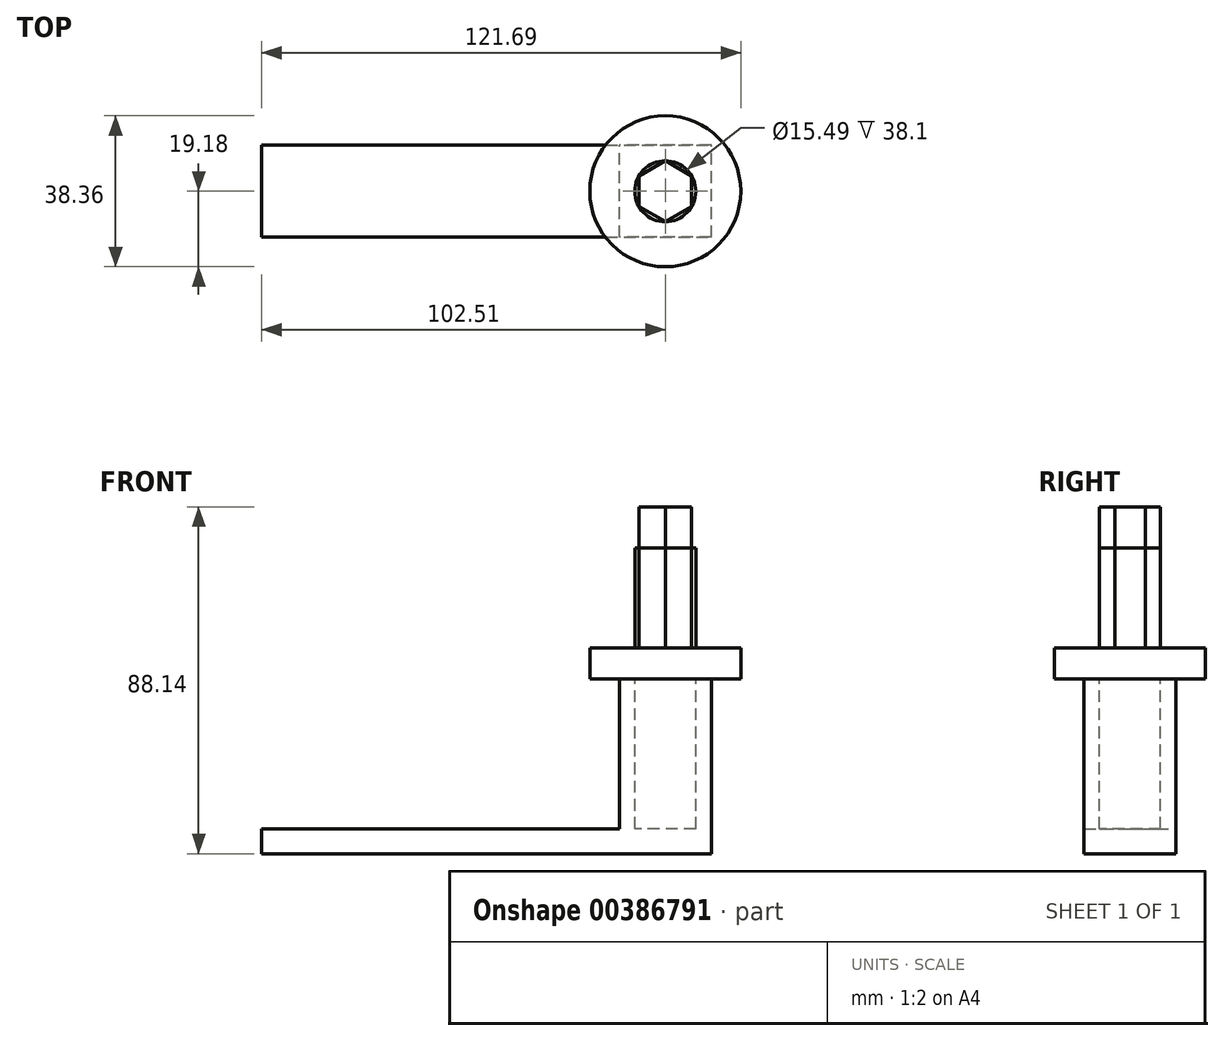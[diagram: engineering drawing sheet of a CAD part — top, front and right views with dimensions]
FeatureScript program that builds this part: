
annotation { "Feature Type Name" : "Feature", "Feature Type Description" : "" }
export const myFeature = defineFeature(function(context is Context, id is Id, definition is map)
    precondition{}
    {
        {
            var Q0;
            Q0=qCreatedBy(makeId("Top.planeOp"),FACE);
            var sketch = newSketch(context, id + "F0", { "sketchPlane" : qUnion([Q0])});
            skCircle(sketch, "E0", {"center": v(0, 0) * mm, "radius": 7.75 * mm});
            skCircle(sketch, "E1.cCircle", {"center": v(0, 0) * mm, "radius": 7.75 * mm, "construction": true});
            skLineSegment(sketch, "E1.0", {"start": v(0, 7.75) * mm, "end": v(6.7, 3.87) * mm});
            skLineSegment(sketch, "E1.1", {"start": v(6.7, 3.87) * mm, "end": v(6.7, -3.87) * mm, "construction": true});
            skLineSegment(sketch, "E1.2", {"start": v(6.7, -3.87) * mm, "end": v(0, -7.75) * mm, "construction": true});
            skLineSegment(sketch, "E1.3", {"start": v(0, -7.75) * mm, "end": v(-6.7, -3.87) * mm, "construction": true});
            skLineSegment(sketch, "E1.4", {"start": v(-6.7, -3.87) * mm, "end": v(-6.7, 3.87) * mm, "construction": true});
            skLineSegment(sketch, "E1.5", {"start": v(-6.7, 3.87) * mm, "end": v(0, 7.75) * mm, "construction": true});
            skLineSegment(sketch, "E2.bottom", {"start": v(-102.55, 11.75) * mm, "end": v(11.75, 11.75) * mm});
            skLineSegment(sketch, "E2.top", {"start": v(-102.55, -11.75) * mm, "end": v(11.75, -11.75) * mm});
            skLineSegment(sketch, "E2.left", {"start": v(-102.55, 11.75) * mm, "end": v(-102.55, -11.75) * mm});
            skLineSegment(sketch, "E2.right", {"start": v(11.75, 11.75) * mm, "end": v(11.75, -11.75) * mm});
            skCircle(sketch, "E3", {"center": v(0, 0) * mm, "radius": 19.18 * mm});
            skLineSegment(sketch, "E4.bottom", {"start": v(11.68, -11.68) * mm, "end": v(-11.68, -11.68) * mm});
            skLineSegment(sketch, "E4.top", {"start": v(11.68, 11.68) * mm, "end": v(-11.68, 11.68) * mm});
            skLineSegment(sketch, "E4.left", {"start": v(11.68, -11.68) * mm, "end": v(11.68, 11.68) * mm});
            skLineSegment(sketch, "E4.right", {"start": v(-11.68, -11.68) * mm, "end": v(-11.68, 11.68) * mm});
            skSolve(sketch);
        }
        {
            var Q0;
            {var subQ0=sQuery(id+"F0.wireOp",EDGE,"E2.right");Q0=makeQuery(id+"F0.imprint","IMPRINT",FACE,{"disambiguationData":[TD([[makeQuery(id+"F0.imprint","IMPRINT",EDGE,{"derivedFrom":subQ0}),1.0]])]});}
            var Q1;
            {var subQ0=sQuery(id+"F0.wireOp",EDGE,"E2.right");Q1=makeQuery(id+"F0.imprint","IMPRINT",FACE,{"disambiguationData":[TD([[makeQuery(id+"F0.imprint","IMPRINT",EDGE,{"derivedFrom":subQ0}),-1.0]])]});}
            var Q2;
            Q2=makeQuery(id+"F0.imprint","IMPRINT",FACE,{"disambiguationData":[TD([[makeQuery(id+"F0.imprint","IMPRINT",EDGE,{"derivedFrom":sQuery(id+"F0.wireOp",EDGE,"E4.bottom")}),-1.0]])]});
            var Q3;
            {var subQ0=sQuery(id+"F0.wireOp",EDGE,"E1.0");Q3=makeQuery(id+"F0.imprint","IMPRINT",FACE,{"disambiguationData":[TD([[makeQuery(id+"F0.imprint","IMPRINT",EDGE,{"derivedFrom":subQ0}),-1.0]])]});}
            var Q4;
            {var subQ0=sQuery(id+"F0.wireOp",EDGE,"E1.0");Q4=makeQuery(id+"F0.imprint","IMPRINT",FACE,{"disambiguationData":[TD([[makeQuery(id+"F0.imprint","IMPRINT",EDGE,{"derivedFrom":subQ0}),1.0]])]});}
            extrude(context, id + "F1", {"entities" : qUnion([Q0, Q1, Q2, Q3, Q4]), "depth" : 7.87 * mm});
        }
        {
            var Q0;
            Q0=makeQuery(id+"F1.opExtrude","CAP_FACE",FACE,{"disambiguationData":[OSD([sQuery(id+"F0.wireOp",EDGE,"E0"),sQuery(id+"F0.wireOp",EDGE,"E3")])],"isStart":false});
            var sketch = newSketch(context, id + "F2", { "sketchPlane" : qUnion([Q0])});
            skCircle(sketch, "E5", {"center": v(0, 0) * mm, "radius": 7.75 * mm});
            skCircle(sketch, "E6.cCircle", {"center": v(0, 0) * mm, "radius": 7.75 * mm, "construction": true});
            skLineSegment(sketch, "E6.0", {"start": v(0, 7.75) * mm, "end": v(6.7, 3.87) * mm});
            skLineSegment(sketch, "E6.1", {"start": v(6.7, 3.87) * mm, "end": v(6.7, -3.87) * mm});
            skLineSegment(sketch, "E6.2", {"start": v(6.7, -3.87) * mm, "end": v(0, -7.75) * mm});
            skLineSegment(sketch, "E6.3", {"start": v(0, -7.75) * mm, "end": v(-6.7, -3.87) * mm});
            skLineSegment(sketch, "E6.4", {"start": v(-6.7, -3.87) * mm, "end": v(-6.7, 3.87) * mm});
            skLineSegment(sketch, "E6.5", {"start": v(-6.7, 3.87) * mm, "end": v(0, 7.75) * mm});
            skSolve(sketch);
        }
        {
            var Q0;
            Q0=makeQuery(id+"F2.imprint","IMPRINT",FACE,{"disambiguationData":[TD([[makeQuery(id+"F2.imprint","IMPRINT",EDGE,{"derivedFrom":sQuery(id+"F2.wireOp",EDGE,"E6.0")}),-1.0]])]});
            extrude(context, id + "F3", {"entities" : qUnion([Q0]), "depth" : 35.81 * mm});
        }
        {
            var Q0;
            Q0=makeQuery(id+"F0.imprint","IMPRINT",FACE,{"disambiguationData":[TD([[makeQuery(id+"F0.imprint","IMPRINT",EDGE,{"derivedFrom":sQuery(id+"F0.wireOp",EDGE,"E4.bottom")}),-1.0]])]});
            extrude(context, id + "F4", {"entities" : qUnion([Q0]), "operationType" : NewBodyOperationType.ADD, "depth" : -38.1 * mm});
        }
        {
            var Q0;
            Q0=makeQuery(id+"F4.opExtrude","CAP_FACE",FACE,{"disambiguationData":[OSD([sQuery(id+"F0.wireOp",EDGE,"E0"),sQuery(id+"F0.wireOp",EDGE,"E4.bottom"),sQuery(id+"F0.wireOp",EDGE,"E4.top"),sQuery(id+"F0.wireOp",EDGE,"E4.left"),sQuery(id+"F0.wireOp",EDGE,"E4.right")])],"isStart":false});
            var sketch = newSketch(context, id + "F5", { "sketchPlane" : qUnion([Q0])});
            skLineSegment(sketch, "E7.bottom", {"start": v(-102.5, 11.68) * mm, "end": v(11.68, 11.68) * mm});
            skLineSegment(sketch, "E7.top", {"start": v(-102.5, -11.68) * mm, "end": v(11.68, -11.68) * mm});
            skLineSegment(sketch, "E7.left", {"start": v(-102.5, 11.68) * mm, "end": v(-102.5, -11.68) * mm});
            skLineSegment(sketch, "E7.right", {"start": v(11.68, 11.68) * mm, "end": v(11.68, -11.68) * mm});
            skSolve(sketch);
        }
        {
            var Q0;
            {var subQ2=sQuery(id+"F5.wireOp",EDGE,"E7.left");Q0=makeQuery(id+"F5.imprint","IMPRINT",FACE,{"disambiguationData":[TD([[makeQuery(id+"F5.imprint","IMPRINT",EDGE,{"derivedFrom":subQ2}),1.0]])]});}
            var Q1;
            {var subQ0=sQuery(id+"F5.wireOp",EDGE,"E7.right");Q1=makeQuery(id+"F5.imprint","IMPRINT",FACE,{"disambiguationData":[TD([[makeQuery(id+"F5.imprint","IMPRINT",EDGE,{"derivedFrom":subQ0}),-1.0]])]});}
            var Q2;
            Q2=makeQuery(id+"F5.imprint","IMPRINT",FACE,{"disambiguationData":[TD([[makeQuery(id+"F5.imprint","IMPRINT",EDGE,{"derivedFrom":makeQuery(id+"F4.opExtrude","CAP_EDGE",EDGE,{"disambiguationData":[OSD([sQuery(id+"F0.wireOp",EDGE,"E0")])],"isStart":false})}),-1.0]])]});
            extrude(context, id + "F6", {"entities" : qUnion([Q0, Q1, Q2]), "operationType" : NewBodyOperationType.ADD, "depth" : 6.35 * mm});
        }
        {
            var Q0;
            Q0=makeQuery(id+"F2.imprint","IMPRINT",FACE,{"disambiguationData":[TD([[makeQuery(id+"F2.imprint","IMPRINT",EDGE,{"derivedFrom":makeQuery(id+"F1.opExtrude","CAP_EDGE",EDGE,{"disambiguationData":[OSD([sQuery(id+"F0.wireOp",EDGE,"E3")])],"isStart":false})}),1.0]])]});
            var sketch = newSketch(context, id + "F7", { "sketchPlane" : qUnion([Q0])});
            skSolve(sketch);
        }
        {
            var Q0;
            {var subQ2=sQuery(id+"F2.wireOp",EDGE,"E5");var subQ6=sQuery(id+"F2.wireOp",EDGE,"E6.5");var subQ8=sQuery(id+"F2.wireOp",EDGE,"E6.0");var subQ9=makeQuery(id+"F2.imprint","INTERSECT",VERTEX,{"derivedFrom":[subQ2,subQ8,subQ6]});Q0=makeQuery(id+"F7.imprint","IMPRINT",FACE,{"disambiguationData":[TD([[makeQuery(id+"F7.imprint","IMPRINT",EDGE,{"derivedFrom":makeQuery(id+"F2.imprint","IMPRINT",EDGE,{"disambiguationData":[TD([[subQ9,1.0]])],"derivedFrom":subQ2})}),1.0]])]});}
            var Q1;
            Q1=sQuery(id+"F2.wireOp",EDGE,"E5");
            extrude(context, id + "F8", {"entities" : qUnion([Q0]), "surfaceEntities" : qUnion([Q1]), "depth" : 25.4 * mm, "offsetDistance" : 25.4 * mm});
        }
    });
